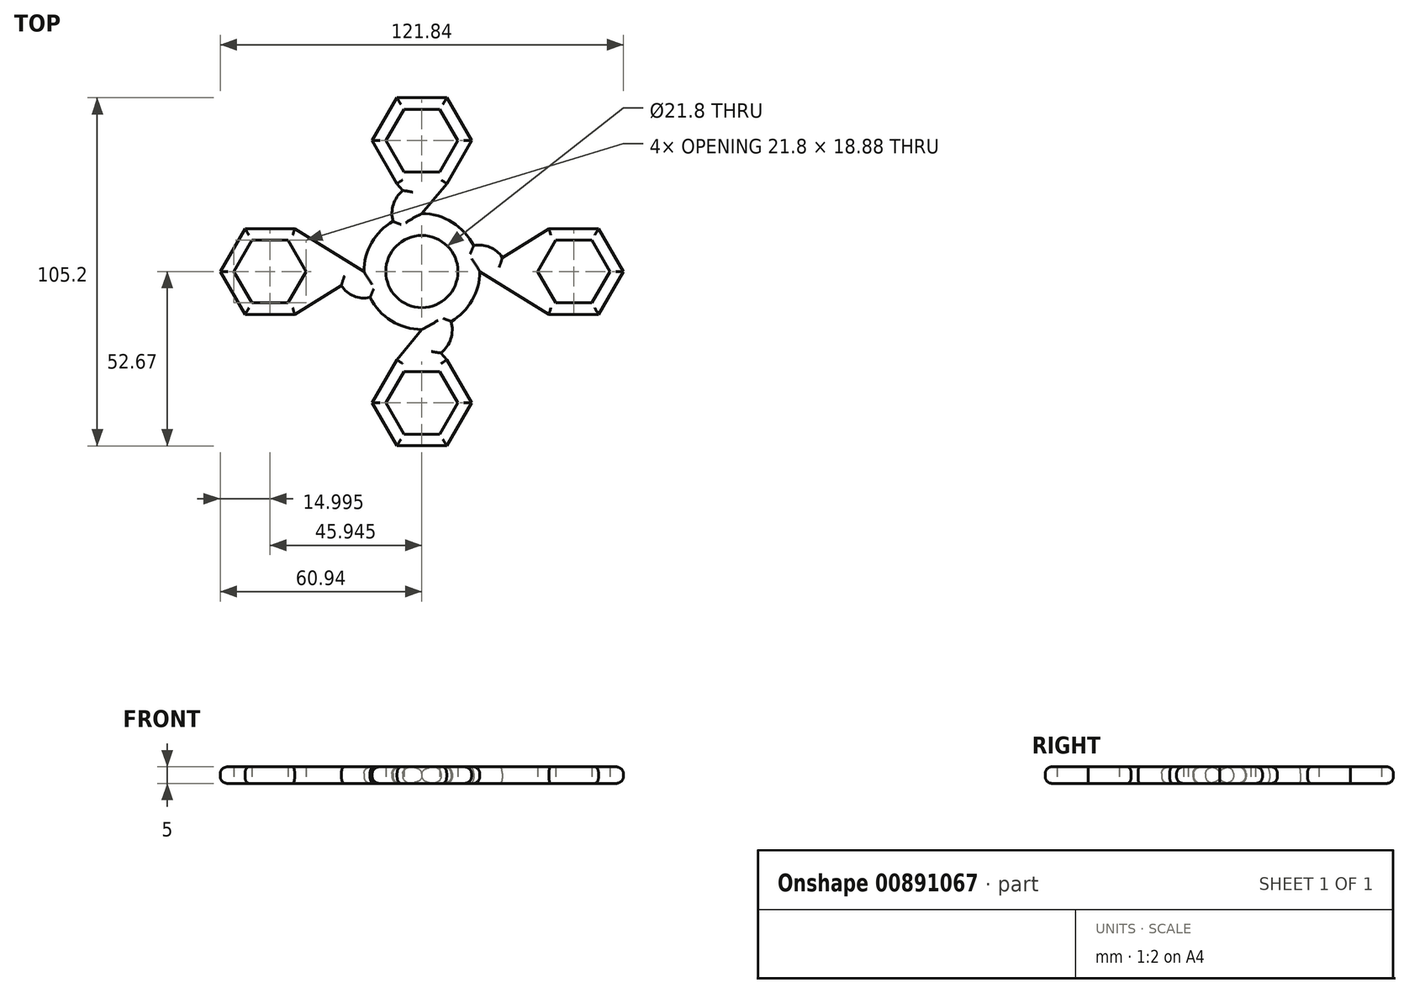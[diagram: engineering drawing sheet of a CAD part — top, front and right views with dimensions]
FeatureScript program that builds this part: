
annotation { "Feature Type Name" : "Feature", "Feature Type Description" : "" }
export const myFeature = defineFeature(function(context is Context, id is Id, definition is map)
    precondition{}
    {
        {
            var Q0;
            Q0=qCreatedBy(makeId("Top.planeOp"),FACE);
            var sketch = newSketch(context, id + "F0", { "sketchPlane" : qUnion([Q0])});
            skCircle(sketch, "E0", {"center": v(0, 0) * mm, "radius": 10.9 * mm});
            skCircle(sketch, "E1.cCircle", {"center": v(45.9, 0) * mm, "radius": 9.44 * mm, "construction": true});
            skLineSegment(sketch, "E1.0", {"start": v(40.45, 9.44) * mm, "end": v(51.35, 9.44) * mm});
            skLineSegment(sketch, "E1.1", {"start": v(51.35, 9.44) * mm, "end": v(56.8, 0) * mm});
            skLineSegment(sketch, "E1.2", {"start": v(56.8, 0) * mm, "end": v(51.35, -9.44) * mm});
            skLineSegment(sketch, "E1.3", {"start": v(51.35, -9.44) * mm, "end": v(40.45, -9.44) * mm});
            skLineSegment(sketch, "E1.4", {"start": v(40.45, -9.44) * mm, "end": v(35, 0) * mm});
            skLineSegment(sketch, "E1.5", {"start": v(35, 0) * mm, "end": v(40.45, 9.44) * mm});
            skPoint(sketch, "E1.0.midPoint", {"position": v(45.9, 9.44) * mm});
            skLineSegment(sketch, "E2", {"start": v(0, 0) * mm, "end": v(35, 0) * mm});
            skLineSegment(sketch, "E3", {"start": v(0, 0) * mm, "end": v(-35, 0) * mm});
            skCircle(sketch, "E4.cCircle", {"center": v(-45.94, 0) * mm, "radius": 9.44 * mm, "construction": true});
            skLineSegment(sketch, "E4.0", {"start": v(-51.4, 9.44) * mm, "end": v(-40.5, 9.44) * mm});
            skLineSegment(sketch, "E4.1", {"start": v(-40.5, 9.44) * mm, "end": v(-35.04, 0) * mm});
            skLineSegment(sketch, "E4.2", {"start": v(-35.04, 0) * mm, "end": v(-40.5, -9.44) * mm});
            skLineSegment(sketch, "E4.3", {"start": v(-40.5, -9.44) * mm, "end": v(-51.4, -9.44) * mm});
            skLineSegment(sketch, "E4.4", {"start": v(-51.4, -9.44) * mm, "end": v(-56.84, 0) * mm});
            skLineSegment(sketch, "E4.5", {"start": v(-56.84, 0) * mm, "end": v(-51.4, 9.44) * mm});
            skPoint(sketch, "E4.0.midPoint", {"position": v(-45.94, 9.44) * mm});
            skLineSegment(sketch, "E5", {"start": v(0, 0) * mm, "end": v(0, 30) * mm});
            skLineSegment(sketch, "E6", {"start": v(0, 30) * mm, "end": v(0, -30) * mm});
            skCircle(sketch, "E7.cCircle", {"center": v(0, -39.68) * mm, "radius": 9.44 * mm, "construction": true});
            skLineSegment(sketch, "E7.0", {"start": v(-5.45, -30.24) * mm, "end": v(5.45, -30.24) * mm});
            skLineSegment(sketch, "E7.1", {"start": v(5.45, -30.24) * mm, "end": v(10.9, -39.68) * mm});
            skLineSegment(sketch, "E7.2", {"start": v(10.9, -39.68) * mm, "end": v(5.45, -49.12) * mm});
            skLineSegment(sketch, "E7.3", {"start": v(5.45, -49.12) * mm, "end": v(-5.45, -49.12) * mm});
            skLineSegment(sketch, "E7.4", {"start": v(-5.45, -49.12) * mm, "end": v(-10.9, -39.68) * mm});
            skLineSegment(sketch, "E7.5", {"start": v(-10.9, -39.68) * mm, "end": v(-5.45, -30.24) * mm});
            skPoint(sketch, "E7.0.midPoint", {"position": v(0, -30.24) * mm});
            skCircle(sketch, "E8.cCircle", {"center": v(0, 39.54) * mm, "radius": 9.44 * mm, "construction": true});
            skLineSegment(sketch, "E8.0", {"start": v(-5.45, 48.98) * mm, "end": v(5.45, 48.98) * mm});
            skLineSegment(sketch, "E8.1", {"start": v(5.45, 48.98) * mm, "end": v(10.9, 39.54) * mm});
            skLineSegment(sketch, "E8.2", {"start": v(10.9, 39.54) * mm, "end": v(5.45, 30.1) * mm});
            skLineSegment(sketch, "E8.3", {"start": v(5.45, 30.1) * mm, "end": v(-5.45, 30.1) * mm});
            skLineSegment(sketch, "E8.4", {"start": v(-5.45, 30.1) * mm, "end": v(-10.9, 39.54) * mm});
            skLineSegment(sketch, "E8.5", {"start": v(-10.9, 39.54) * mm, "end": v(-5.45, 48.98) * mm});
            skPoint(sketch, "E8.0.midPoint", {"position": v(0, 48.98) * mm});
            skCircle(sketch, "E9", {"center": v(0, 0) * mm, "radius": 17.5 * mm});
            skCircle(sketch, "E10.cCircle", {"center": v(-45.94, 0) * mm, "radius": 13 * mm, "construction": true});
            skLineSegment(sketch, "E10.0", {"start": v(-53.44, 13) * mm, "end": v(-38.44, 13) * mm});
            skLineSegment(sketch, "E10.1", {"start": v(-38.44, 13) * mm, "end": v(-30.94, 0) * mm});
            skLineSegment(sketch, "E10.2", {"start": v(-30.94, 0) * mm, "end": v(-38.44, -13) * mm});
            skLineSegment(sketch, "E10.3", {"start": v(-38.44, -13) * mm, "end": v(-53.44, -13) * mm});
            skLineSegment(sketch, "E10.4", {"start": v(-53.44, -13) * mm, "end": v(-60.94, 0) * mm});
            skLineSegment(sketch, "E10.5", {"start": v(-60.94, 0) * mm, "end": v(-53.44, 13) * mm});
            skPoint(sketch, "E10.0.midPoint", {"position": v(-45.94, 13) * mm});
            skCircle(sketch, "E11.cCircle", {"center": v(0, 39.54) * mm, "radius": 13 * mm, "construction": true});
            skLineSegment(sketch, "E11.0", {"start": v(-7.5, 52.53) * mm, "end": v(7.5, 52.53) * mm});
            skLineSegment(sketch, "E11.1", {"start": v(7.5, 52.53) * mm, "end": v(15, 39.54) * mm});
            skLineSegment(sketch, "E11.2", {"start": v(15, 39.54) * mm, "end": v(7.5, 26.55) * mm});
            skLineSegment(sketch, "E11.3", {"start": v(7.5, 26.55) * mm, "end": v(-7.5, 26.55) * mm});
            skLineSegment(sketch, "E11.4", {"start": v(-7.5, 26.55) * mm, "end": v(-15, 39.54) * mm});
            skLineSegment(sketch, "E11.5", {"start": v(-15, 39.54) * mm, "end": v(-7.5, 52.53) * mm});
            skPoint(sketch, "E11.0.midPoint", {"position": v(0, 52.53) * mm});
            skCircle(sketch, "E12.cCircle", {"center": v(45.9, 0) * mm, "radius": 13 * mm, "construction": true});
            skLineSegment(sketch, "E12.0", {"start": v(38.4, 13) * mm, "end": v(53.4, 13) * mm});
            skLineSegment(sketch, "E12.1", {"start": v(53.4, 13) * mm, "end": v(60.9, 0) * mm});
            skLineSegment(sketch, "E12.2", {"start": v(60.9, 0) * mm, "end": v(53.4, -13) * mm});
            skLineSegment(sketch, "E12.3", {"start": v(53.4, -13) * mm, "end": v(38.4, -13) * mm});
            skLineSegment(sketch, "E12.4", {"start": v(38.4, -13) * mm, "end": v(30.9, 0) * mm});
            skLineSegment(sketch, "E12.5", {"start": v(30.9, 0) * mm, "end": v(38.4, 13) * mm});
            skPoint(sketch, "E12.0.midPoint", {"position": v(45.9, 13) * mm});
            skCircle(sketch, "E13.cCircle", {"center": v(0, -39.68) * mm, "radius": 13 * mm, "construction": true});
            skLineSegment(sketch, "E13.0", {"start": v(-7.5, -26.69) * mm, "end": v(7.5, -26.69) * mm});
            skLineSegment(sketch, "E13.1", {"start": v(7.5, -26.69) * mm, "end": v(15, -39.68) * mm});
            skLineSegment(sketch, "E13.2", {"start": v(15, -39.68) * mm, "end": v(7.5, -52.67) * mm});
            skLineSegment(sketch, "E13.3", {"start": v(7.5, -52.67) * mm, "end": v(-7.5, -52.67) * mm});
            skLineSegment(sketch, "E13.4", {"start": v(-7.5, -52.67) * mm, "end": v(-15, -39.68) * mm});
            skLineSegment(sketch, "E13.5", {"start": v(-15, -39.68) * mm, "end": v(-7.5, -26.69) * mm});
            skPoint(sketch, "E13.0.midPoint", {"position": v(0, -26.69) * mm});
            skLineSegment(sketch, "E14", {"start": v(-7.5, 26.55) * mm, "end": v(0, 17.5) * mm});
            skLineSegment(sketch, "E15", {"start": v(0, 17.5) * mm, "end": v(7.5, 26.55) * mm});
            skLineSegment(sketch, "E16", {"start": v(-7.5, -26.69) * mm, "end": v(0, -17.5) * mm});
            skLineSegment(sketch, "E17", {"start": v(0, -17.5) * mm, "end": v(7.5, -26.69) * mm});
            skLineSegment(sketch, "E18", {"start": v(38.4, -13) * mm, "end": v(17.5, 0) * mm});
            skLineSegment(sketch, "E19", {"start": v(17.5, 0) * mm, "end": v(38.4, 13) * mm});
            skLineSegment(sketch, "E20", {"start": v(-17.5, 0) * mm, "end": v(-38.44, -13) * mm});
            skLineSegment(sketch, "E21", {"start": v(-17.5, 0) * mm, "end": v(-38.44, 13) * mm});
            skLineSegment(sketch, "E22", {"start": v(-17.5, 0) * mm, "end": v(-22.5, 0) * mm});
            skLineSegment(sketch, "E23", {"start": v(17.5, 0) * mm, "end": v(22.5, 0) * mm});
            skArc(sketch, "E24", {"start": v(0, -26.69) * mm, "mid": v(7.3, -23.08) * mm, "end": v(8.86, -15.09) * mm});
            skArc(sketch, "E25", {"start": v(0, -26.69) * mm, "mid": v(-7.3, -23.08) * mm, "end": v(-8.86, -15.09) * mm});
            skArc(sketch, "E26", {"start": v(0, 26.55) * mm, "mid": v(7.18, 23) * mm, "end": v(8.74, 15.16) * mm});
            skArc(sketch, "E27", {"start": v(0, 26.55) * mm, "mid": v(-7.18, 23) * mm, "end": v(-8.74, 15.16) * mm});
            skPoint(sketch, "E28", {"position": v(27.95, -6.5) * mm});
            skPoint(sketch, "E29", {"position": v(27.95, 6.5) * mm});
            skLineSegment(sketch, "E30", {"start": v(17.5, 0) * mm, "end": v(25.5, 0) * mm});
            skLineSegment(sketch, "E31", {"start": v(-17.5, 0) * mm, "end": v(-25.5, 0) * mm});
            skArc(sketch, "E32", {"start": v(25.5, 0) * mm, "mid": v(22.47, -6.27) * mm, "end": v(15.67, -7.79) * mm});
            skArc(sketch, "E33", {"start": v(25.5, 0) * mm, "mid": v(22.47, 6.27) * mm, "end": v(15.67, 7.79) * mm});
            skArc(sketch, "E34", {"start": v(-25.5, 0) * mm, "mid": v(-22.47, -6.27) * mm, "end": v(-15.67, -7.79) * mm});
            skArc(sketch, "E35", {"start": v(-25.5, 0) * mm, "mid": v(-22.47, 6.27) * mm, "end": v(-15.67, 7.79) * mm});
            skSolve(sketch);
        }
        {
            var Q0;
            Q0=makeQuery(id+"F0.imprint","IMPRINT",FACE,{"disambiguationData":[TD([[makeQuery(id+"F0.imprint","IMPRINT",EDGE,{"derivedFrom":sQuery(id+"F0.wireOp",EDGE,"E4.0")}),1.0]])]});
            var Q1;
            {var subQ4=sQuery(id+"F0.wireOp",EDGE,"E0");var subQ6=sQuery(id+"F0.wireOp",EDGE,"E5");var subQ7=makeQuery(id+"F0.imprint","INTERSECT",VERTEX,{"derivedFrom":[subQ4,subQ6]});Q1=makeQuery(id+"F0.imprint","IMPRINT",FACE,{"disambiguationData":[TD([[makeQuery(id+"F0.imprint","IMPRINT",EDGE,{"disambiguationData":[TD([[subQ7,1.0]])],"derivedFrom":subQ4}),-1.0]])]});}
            var Q2;
            {var subQ3=sQuery(id+"F0.wireOp",EDGE,"E0");var subQ6=sQuery(id+"F0.wireOp",EDGE,"E2");var subQ8=makeQuery(id+"F0.imprint","INTERSECT",VERTEX,{"derivedFrom":[subQ3,subQ6]});Q2=makeQuery(id+"F0.imprint","IMPRINT",FACE,{"disambiguationData":[TD([[makeQuery(id+"F0.imprint","IMPRINT",EDGE,{"disambiguationData":[TD([[subQ8,1.0]])],"derivedFrom":subQ3}),-1.0]])]});}
            var Q3;
            {var subQ1=sQuery(id+"F0.wireOp",EDGE,"E5");var subQ4=sQuery(id+"F0.wireOp",EDGE,"E0");var subQ5=makeQuery(id+"F0.imprint","INTERSECT",VERTEX,{"derivedFrom":[subQ4,subQ1]});Q3=makeQuery(id+"F0.imprint","IMPRINT",FACE,{"disambiguationData":[TD([[makeQuery(id+"F0.imprint","IMPRINT",EDGE,{"disambiguationData":[TD([[subQ5,-1.0]])],"derivedFrom":subQ4}),-1.0]])]});}
            var Q4;
            Q4=makeQuery(id+"F0.imprint","IMPRINT",FACE,{"disambiguationData":[TD([[makeQuery(id+"F0.imprint","IMPRINT",EDGE,{"derivedFrom":sQuery(id+"F0.wireOp",EDGE,"E8.0")}),1.0]])]});
            var Q5;
            Q5=makeQuery(id+"F0.imprint","IMPRINT",FACE,{"disambiguationData":[TD([[makeQuery(id+"F0.imprint","IMPRINT",EDGE,{"derivedFrom":sQuery(id+"F0.wireOp",EDGE,"E1.0")}),1.0]])]});
            var Q6;
            Q6=makeQuery(id+"F0.imprint","IMPRINT",FACE,{"disambiguationData":[TD([[makeQuery(id+"F0.imprint","IMPRINT",EDGE,{"derivedFrom":sQuery(id+"F0.wireOp",EDGE,"E7.0")}),1.0]])]});
            var Q7;
            {var subQ0=sQuery(id+"F0.wireOp",EDGE,"E15");var subQ3=sQuery(id+"F0.wireOp",EDGE,"E26");var subQ6=makeQuery(id+"F0.imprint","INTERSECT",VERTEX,{"derivedFrom":[subQ0,subQ3]});Q7=qUnion([makeQuery(id+"F0.imprint","IMPRINT",FACE,{"disambiguationData":[TD([[makeQuery(id+"F0.imprint","IMPRINT",EDGE,{"disambiguationData":[TD([[subQ6,1.0]])],"derivedFrom":subQ0}),1.0]])]}),makeQuery(id+"F0.imprint","IMPRINT",FACE,{"disambiguationData":[TD([[makeQuery(id+"F0.imprint","IMPRINT",EDGE,{"disambiguationData":[TD([[subQ6,-1.0]])],"derivedFrom":subQ0}),1.0]])]})]);}
            var Q8;
            {var subQ0=sQuery(id+"F0.wireOp",EDGE,"E27");var subQ4=sQuery(id+"F0.wireOp",EDGE,"E14");var subQ6=makeQuery(id+"F0.imprint","INTERSECT",VERTEX,{"derivedFrom":[subQ4,subQ0]});Q8=qUnion([makeQuery(id+"F0.imprint","IMPRINT",FACE,{"disambiguationData":[TD([[makeQuery(id+"F0.imprint","IMPRINT",EDGE,{"disambiguationData":[TD([[subQ6,-1.0]])],"derivedFrom":subQ4}),1.0]])]}),makeQuery(id+"F0.imprint","IMPRINT",FACE,{"disambiguationData":[TD([[makeQuery(id+"F0.imprint","IMPRINT",EDGE,{"disambiguationData":[TD([[subQ6,1.0]])],"derivedFrom":subQ4}),1.0]])]})]);}
            var Q9;
            {var subQ0=sQuery(id+"F0.wireOp",EDGE,"E17");var subQ3=sQuery(id+"F0.wireOp",EDGE,"E24");var subQ6=makeQuery(id+"F0.imprint","INTERSECT",VERTEX,{"derivedFrom":[subQ0,subQ3]});Q9=qUnion([makeQuery(id+"F0.imprint","IMPRINT",FACE,{"disambiguationData":[TD([[makeQuery(id+"F0.imprint","IMPRINT",EDGE,{"disambiguationData":[TD([[subQ6,1.0]])],"derivedFrom":subQ0}),-1.0]])]}),makeQuery(id+"F0.imprint","IMPRINT",FACE,{"disambiguationData":[TD([[makeQuery(id+"F0.imprint","IMPRINT",EDGE,{"disambiguationData":[TD([[subQ6,-1.0]])],"derivedFrom":subQ0}),-1.0]])]})]);}
            var Q10;
            {var subQ0=sQuery(id+"F0.wireOp",EDGE,"E16");var subQ3=sQuery(id+"F0.wireOp",EDGE,"E25");var subQ6=makeQuery(id+"F0.imprint","INTERSECT",VERTEX,{"derivedFrom":[subQ0,subQ3]});Q10=qUnion([makeQuery(id+"F0.imprint","IMPRINT",FACE,{"disambiguationData":[TD([[makeQuery(id+"F0.imprint","IMPRINT",EDGE,{"disambiguationData":[TD([[subQ6,1.0]])],"derivedFrom":subQ0}),-1.0]])]}),makeQuery(id+"F0.imprint","IMPRINT",FACE,{"disambiguationData":[TD([[makeQuery(id+"F0.imprint","IMPRINT",EDGE,{"disambiguationData":[TD([[subQ6,-1.0]])],"derivedFrom":subQ0}),-1.0]])]})]);}
            var Q11;
            {var subQ3=sQuery(id+"F0.wireOp",EDGE,"E10.2");Q11=makeQuery(id+"F0.imprint","IMPRINT",FACE,{"disambiguationData":[TD([[makeQuery(id+"F0.imprint","IMPRINT",EDGE,{"derivedFrom":subQ3}),1.0]])]});}
            var Q12;
            {var subQ3=sQuery(id+"F0.wireOp",EDGE,"E10.1");Q12=makeQuery(id+"F0.imprint","IMPRINT",FACE,{"disambiguationData":[TD([[makeQuery(id+"F0.imprint","IMPRINT",EDGE,{"derivedFrom":subQ3}),1.0]])]});}
            var Q13;
            {var subQ3=sQuery(id+"F0.wireOp",EDGE,"E12.4");Q13=makeQuery(id+"F0.imprint","IMPRINT",FACE,{"disambiguationData":[TD([[makeQuery(id+"F0.imprint","IMPRINT",EDGE,{"derivedFrom":subQ3}),1.0]])]});}
            var Q14;
            {var subQ3=sQuery(id+"F0.wireOp",EDGE,"E12.5");Q14=makeQuery(id+"F0.imprint","IMPRINT",FACE,{"disambiguationData":[TD([[makeQuery(id+"F0.imprint","IMPRINT",EDGE,{"derivedFrom":subQ3}),1.0]])]});}
            var Q15;
            {var subQ1=sQuery(id+"F0.wireOp",EDGE,"E9");var subQ3=sQuery(id+"F0.wireOp",EDGE,"Ubq4kfX4-oC6w-lFNq-I3q3-88G8mSC7eADd");var subQ4=makeQuery(id+"F0.imprint","INTERSECT",VERTEX,{"derivedFrom":[subQ1,subQ3]});Q15=makeQuery(id+"F0.imprint","IMPRINT",FACE,{"disambiguationData":[TD([[makeQuery(id+"F0.imprint","IMPRINT",EDGE,{"disambiguationData":[TD([[subQ4,1.0]])],"derivedFrom":subQ3}),1.0]])]});}
            var Q16;
            {var subQ0=sQuery(id+"F0.wireOp",EDGE,"E22");Q16=makeQuery(id+"F0.imprint","IMPRINT",FACE,{"disambiguationData":[TD([[makeQuery(id+"F0.imprint","IMPRINT",EDGE,{"derivedFrom":subQ0}),1.0]])]});}
            var Q17;
            {var subQ1=sQuery(id+"F0.wireOp",EDGE,"E9");var subQ3=sQuery(id+"F0.wireOp",EDGE,"DwJBgmho-QLLy-2BSY-i2pv-QXPFVA0WSpVR");var subQ4=makeQuery(id+"F0.imprint","INTERSECT",VERTEX,{"derivedFrom":[subQ1,subQ3]});Q17=makeQuery(id+"F0.imprint","IMPRINT",FACE,{"disambiguationData":[TD([[makeQuery(id+"F0.imprint","IMPRINT",EDGE,{"disambiguationData":[TD([[subQ4,1.0]])],"derivedFrom":subQ3}),-1.0]])]});}
            var Q18;
            {var subQ0=sQuery(id+"F0.wireOp",EDGE,"E22");Q18=makeQuery(id+"F0.imprint","IMPRINT",FACE,{"disambiguationData":[TD([[makeQuery(id+"F0.imprint","IMPRINT",EDGE,{"derivedFrom":subQ0}),-1.0]])]});}
            var Q19;
            {var subQ1=sQuery(id+"F0.wireOp",EDGE,"E9");var subQ3=sQuery(id+"F0.wireOp",EDGE,"ud0qLV0T-u8xm-Fev3-eQ3F-uhF6uLOVjt4z");var subQ4=makeQuery(id+"F0.imprint","INTERSECT",VERTEX,{"derivedFrom":[subQ1,subQ3]});Q19=makeQuery(id+"F0.imprint","IMPRINT",FACE,{"disambiguationData":[TD([[makeQuery(id+"F0.imprint","IMPRINT",EDGE,{"disambiguationData":[TD([[subQ4,1.0]])],"derivedFrom":subQ3}),1.0]])]});}
            var Q20;
            {var subQ0=sQuery(id+"F0.wireOp",EDGE,"E23");Q20=makeQuery(id+"F0.imprint","IMPRINT",FACE,{"disambiguationData":[TD([[makeQuery(id+"F0.imprint","IMPRINT",EDGE,{"derivedFrom":subQ0}),1.0]])]});}
            var Q21;
            {var subQ0=sQuery(id+"F0.wireOp",EDGE,"E23");Q21=makeQuery(id+"F0.imprint","IMPRINT",FACE,{"disambiguationData":[TD([[makeQuery(id+"F0.imprint","IMPRINT",EDGE,{"derivedFrom":subQ0}),-1.0]])]});}
            var Q22;
            {var subQ1=sQuery(id+"F0.wireOp",EDGE,"E9");var subQ3=sQuery(id+"F0.wireOp",EDGE,"Qvp8duAn-RZq8-JCAh-Xm4F-s16nUtTtBb3N");var subQ4=makeQuery(id+"F0.imprint","INTERSECT",VERTEX,{"derivedFrom":[subQ1,subQ3]});Q22=makeQuery(id+"F0.imprint","IMPRINT",FACE,{"disambiguationData":[TD([[makeQuery(id+"F0.imprint","IMPRINT",EDGE,{"disambiguationData":[TD([[subQ4,1.0]])],"derivedFrom":subQ3}),-1.0]])]});}
            var Q23;
            {var subQ1=sQuery(id+"F0.wireOp",EDGE,"E9");var subQ3=sQuery(id+"F0.wireOp",EDGE,"c0TzAWUU-cxwK-REM3-tjBK-XptVohU1FABc");var subQ4=makeQuery(id+"F0.imprint","INTERSECT",VERTEX,{"derivedFrom":[subQ1,subQ3]});Q23=makeQuery(id+"F0.imprint","IMPRINT",FACE,{"disambiguationData":[TD([[makeQuery(id+"F0.imprint","IMPRINT",EDGE,{"disambiguationData":[TD([[subQ4,1.0]])],"derivedFrom":subQ3}),-1.0]])]});}
            var Q24;
            {var subQ1=sQuery(id+"F0.wireOp",EDGE,"E9");var subQ3=sQuery(id+"F0.wireOp",EDGE,"k8nK72Cl-iwD2-dbTf-OI5i-pcYR12xtiAX6");var subQ4=makeQuery(id+"F0.imprint","INTERSECT",VERTEX,{"derivedFrom":[subQ1,subQ3]});Q24=makeQuery(id+"F0.imprint","IMPRINT",FACE,{"disambiguationData":[TD([[makeQuery(id+"F0.imprint","IMPRINT",EDGE,{"disambiguationData":[TD([[subQ4,1.0]])],"derivedFrom":subQ3}),1.0]])]});}
            var Q25;
            {var subQ0=sQuery(id+"F0.wireOp",EDGE,"E27");var subQ3=sQuery(id+"F0.wireOp",EDGE,"E14");var subQ5=makeQuery(id+"F0.imprint","INTERSECT",VERTEX,{"derivedFrom":[subQ3,subQ0]});Q25=makeQuery(id+"F0.imprint","IMPRINT",FACE,{"disambiguationData":[TD([[makeQuery(id+"F0.imprint","IMPRINT",EDGE,{"disambiguationData":[TD([[subQ5,-1.0]])],"derivedFrom":subQ3}),1.0]])]});}
            var Q26;
            {var subQ0=sQuery(id+"F0.wireOp",EDGE,"E26");var subQ3=sQuery(id+"F0.wireOp",EDGE,"E15");var subQ5=makeQuery(id+"F0.imprint","INTERSECT",VERTEX,{"derivedFrom":[subQ3,subQ0]});Q26=makeQuery(id+"F0.imprint","IMPRINT",FACE,{"disambiguationData":[TD([[makeQuery(id+"F0.imprint","IMPRINT",EDGE,{"disambiguationData":[TD([[subQ5,1.0]])],"derivedFrom":subQ3}),1.0]])]});}
            var Q27;
            {var subQ0=sQuery(id+"F0.wireOp",EDGE,"E16");var subQ3=sQuery(id+"F0.wireOp",EDGE,"E25");var subQ5=makeQuery(id+"F0.imprint","INTERSECT",VERTEX,{"derivedFrom":[subQ0,subQ3]});Q27=makeQuery(id+"F0.imprint","IMPRINT",FACE,{"disambiguationData":[TD([[makeQuery(id+"F0.imprint","IMPRINT",EDGE,{"disambiguationData":[TD([[subQ5,-1.0]])],"derivedFrom":subQ3}),-1.0]])]});}
            var Q28;
            {var subQ1=sQuery(id+"F0.wireOp",EDGE,"E9");var subQ3=sQuery(id+"F0.wireOp",EDGE,"E24");var subQ4=makeQuery(id+"F0.imprint","INTERSECT",VERTEX,{"derivedFrom":[subQ1,subQ3]});Q28=makeQuery(id+"F0.imprint","IMPRINT",FACE,{"disambiguationData":[TD([[makeQuery(id+"F0.imprint","IMPRINT",EDGE,{"disambiguationData":[TD([[subQ4,1.0]])],"derivedFrom":subQ3}),1.0]])]});}
            var Q29;
            {var subQ1=sQuery(id+"F0.wireOp",EDGE,"E9");var subQ3=sQuery(id+"F0.wireOp",EDGE,"E32");var subQ4=makeQuery(id+"F0.imprint","INTERSECT",VERTEX,{"derivedFrom":[subQ1,subQ3]});Q29=makeQuery(id+"F0.imprint","IMPRINT",FACE,{"disambiguationData":[TD([[makeQuery(id+"F0.imprint","IMPRINT",EDGE,{"disambiguationData":[TD([[subQ4,1.0]])],"derivedFrom":subQ3}),-1.0]])]});}
            var Q30;
            {var subQ0=sQuery(id+"F0.wireOp",EDGE,"E19");var subQ3=sQuery(id+"F0.wireOp",EDGE,"E33");var subQ5=makeQuery(id+"F0.imprint","INTERSECT",VERTEX,{"derivedFrom":[subQ0,subQ3]});Q30=makeQuery(id+"F0.imprint","IMPRINT",FACE,{"disambiguationData":[TD([[makeQuery(id+"F0.imprint","IMPRINT",EDGE,{"disambiguationData":[TD([[subQ5,-1.0]])],"derivedFrom":subQ3}),1.0]])]});}
            var Q31;
            {var subQ1=sQuery(id+"F0.wireOp",EDGE,"E2");var subQ3=makeQuery(id+"F0.imprint","IMPRINT",VERTEX,{"derivedFrom":subQ1});Q31=makeQuery(id+"F0.imprint","IMPRINT",FACE,{"disambiguationData":[TD([[makeQuery(id+"F0.imprint","IMPRINT",EDGE,{"disambiguationData":[TD([[subQ3,-1.0]])],"derivedFrom":subQ1}),1.0]])]});}
            var Q32;
            {var subQ1=sQuery(id+"F0.wireOp",EDGE,"E2");var subQ3=makeQuery(id+"F0.imprint","IMPRINT",VERTEX,{"derivedFrom":subQ1});Q32=makeQuery(id+"F0.imprint","IMPRINT",FACE,{"disambiguationData":[TD([[makeQuery(id+"F0.imprint","IMPRINT",EDGE,{"disambiguationData":[TD([[subQ3,-1.0]])],"derivedFrom":subQ1}),-1.0]])]});}
            var Q33;
            {var subQ0=sQuery(id+"F0.wireOp",EDGE,"E34");var subQ3=sQuery(id+"F0.wireOp",EDGE,"E20");var subQ5=makeQuery(id+"F0.imprint","INTERSECT",VERTEX,{"derivedFrom":[subQ3,subQ0]});Q33=makeQuery(id+"F0.imprint","IMPRINT",FACE,{"disambiguationData":[TD([[makeQuery(id+"F0.imprint","IMPRINT",EDGE,{"disambiguationData":[TD([[subQ5,-1.0]])],"derivedFrom":subQ0}),1.0]])]});}
            var Q34;
            {var subQ2=sQuery(id+"F0.wireOp",EDGE,"E3");var subQ6=sQuery(id+"F0.wireOp",EDGE,"E0");var subQ8=makeQuery(id+"F0.imprint","INTERSECT",VERTEX,{"derivedFrom":[subQ6,subQ2]});Q34=makeQuery(id+"F0.imprint","IMPRINT",FACE,{"disambiguationData":[TD([[makeQuery(id+"F0.imprint","IMPRINT",EDGE,{"disambiguationData":[TD([[subQ8,-1.0]])],"derivedFrom":subQ6}),-1.0]])]});}
            var Q35;
            {var subQ0=sQuery(id+"F0.wireOp",EDGE,"E3");var subQ1=makeQuery(id+"F0.imprint","IMPRINT",VERTEX,{"derivedFrom":subQ0});Q35=makeQuery(id+"F0.imprint","IMPRINT",FACE,{"disambiguationData":[TD([[makeQuery(id+"F0.imprint","IMPRINT",EDGE,{"disambiguationData":[TD([[subQ1,-1.0]])],"derivedFrom":subQ0}),1.0]])]});}
            var Q36;
            {var subQ0=sQuery(id+"F0.wireOp",EDGE,"E3");var subQ1=makeQuery(id+"F0.imprint","IMPRINT",VERTEX,{"derivedFrom":subQ0});Q36=makeQuery(id+"F0.imprint","IMPRINT",FACE,{"disambiguationData":[TD([[makeQuery(id+"F0.imprint","IMPRINT",EDGE,{"disambiguationData":[TD([[subQ1,-1.0]])],"derivedFrom":subQ0}),-1.0]])]});}
            var Q37;
            {var subQ0=sQuery(id+"F0.wireOp",EDGE,"E35");var subQ3=sQuery(id+"F0.wireOp",EDGE,"E21");var subQ5=makeQuery(id+"F0.imprint","INTERSECT",VERTEX,{"derivedFrom":[subQ3,subQ0]});Q37=makeQuery(id+"F0.imprint","IMPRINT",FACE,{"disambiguationData":[TD([[makeQuery(id+"F0.imprint","IMPRINT",EDGE,{"disambiguationData":[TD([[subQ5,-1.0]])],"derivedFrom":subQ0}),-1.0]])]});}
            var Q38;
            {var subQ0=sQuery(id+"F0.wireOp",EDGE,"E14");var subQ3=sQuery(id+"F0.wireOp",EDGE,"E27");var subQ5=makeQuery(id+"F0.imprint","INTERSECT",VERTEX,{"derivedFrom":[subQ0,subQ3]});Q38=makeQuery(id+"F0.imprint","IMPRINT",FACE,{"disambiguationData":[TD([[makeQuery(id+"F0.imprint","IMPRINT",EDGE,{"disambiguationData":[TD([[subQ5,-1.0]])],"derivedFrom":subQ3}),1.0]])]});}
            var Q39;
            {var subQ1=sQuery(id+"F0.wireOp",EDGE,"E9");var subQ3=sQuery(id+"F0.wireOp",EDGE,"E26");var subQ4=makeQuery(id+"F0.imprint","INTERSECT",VERTEX,{"derivedFrom":[subQ1,subQ3]});Q39=makeQuery(id+"F0.imprint","IMPRINT",FACE,{"disambiguationData":[TD([[makeQuery(id+"F0.imprint","IMPRINT",EDGE,{"disambiguationData":[TD([[subQ4,1.0]])],"derivedFrom":subQ3}),-1.0]])]});}
            extrude(context, id + "F1", {"entities" : qUnion([Q0, Q1, Q2, Q3, Q4, Q5, Q6, Q7, Q8, Q9, Q10, Q11, Q12, Q13, Q14, Q15, Q16, Q17, Q18, Q19, Q20, Q21, Q22, Q23, Q24, Q25, Q26, Q27, Q28, Q29, Q30, Q31, Q32, Q33, Q34, Q35, Q36, Q37, Q38, Q39]), "depth" : 5 * mm, "offsetDistance" : 25 * mm});
        }
        {
            var Q0;
            Q0=makeQuery(id+"F1.opExtrude","CAP_EDGE",EDGE,{"disambiguationData":[OSD([sQuery(id+"F0.wireOp",EDGE,"E25")])],"isStart":false});
            var Q1;
            Q1=makeQuery(id+"F1.opExtrude","CAP_EDGE",EDGE,{"disambiguationData":[OSD([sQuery(id+"F0.wireOp",EDGE,"E16")])],"isStart":false});
            var Q2;
            Q2=makeQuery(id+"F1.opExtrude","CAP_EDGE",EDGE,{"disambiguationData":[OSD([sQuery(id+"F0.wireOp",EDGE,"E13.5")])],"isStart":false});
            var Q3;
            Q3=makeQuery(id+"F1.opExtrude","CAP_EDGE",EDGE,{"disambiguationData":[OSD([sQuery(id+"F0.wireOp",EDGE,"E13.4")])],"isStart":false});
            var Q4;
            Q4=makeQuery(id+"F1.opExtrude","CAP_EDGE",EDGE,{"disambiguationData":[OSD([sQuery(id+"F0.wireOp",EDGE,"E13.3")])],"isStart":false});
            var Q5;
            Q5=makeQuery(id+"F1.opExtrude","CAP_EDGE",EDGE,{"disambiguationData":[OSD([sQuery(id+"F0.wireOp",EDGE,"E13.2")])],"isStart":false});
            var Q6;
            Q6=makeQuery(id+"F1.opExtrude","CAP_EDGE",EDGE,{"disambiguationData":[OSD([sQuery(id+"F0.wireOp",EDGE,"E13.1")])],"isStart":false});
            var Q7;
            Q7=makeQuery(id+"F1.opExtrude","CAP_EDGE",EDGE,{"disambiguationData":[OSD([sQuery(id+"F0.wireOp",EDGE,"E17")])],"isStart":false});
            var Q8;
            Q8=makeQuery(id+"F1.opExtrude","CAP_EDGE",EDGE,{"disambiguationData":[OSD([sQuery(id+"F0.wireOp",EDGE,"E24")])],"isStart":false});
            fillet(context, id + "F2", {"entities" : qUnion([Q0, Q1, Q2, Q3, Q4, Q5, Q6, Q7, Q8]), "radius" : 2 * mm, "tangentPropagation" : true, "allowEdgeOverflow" : false});
        }
        {
            var Q0;
            Q0=makeQuery(id+"F1.opExtrude","CAP_EDGE",EDGE,{"disambiguationData":[OSD([sQuery(id+"F0.wireOp",EDGE,"E13.5")])],"isStart":true});
            var Q1;
            Q1=makeQuery(id+"F1.opExtrude","CAP_EDGE",EDGE,{"disambiguationData":[OSD([sQuery(id+"F0.wireOp",EDGE,"E16")])],"isStart":true});
            var Q2;
            Q2=makeQuery(id+"F1.opExtrude","CAP_EDGE",EDGE,{"disambiguationData":[OSD([sQuery(id+"F0.wireOp",EDGE,"E25")])],"isStart":true});
            var Q3;
            Q3=makeQuery(id+"F1.opExtrude","CAP_EDGE",EDGE,{"disambiguationData":[OSD([sQuery(id+"F0.wireOp",EDGE,"E24")])],"isStart":true});
            var Q4;
            Q4=makeQuery(id+"F1.opExtrude","CAP_EDGE",EDGE,{"disambiguationData":[OSD([sQuery(id+"F0.wireOp",EDGE,"E17")])],"isStart":true});
            var Q5;
            Q5=makeQuery(id+"F1.opExtrude","CAP_EDGE",EDGE,{"disambiguationData":[OSD([sQuery(id+"F0.wireOp",EDGE,"E13.1")])],"isStart":true});
            var Q6;
            Q6=makeQuery(id+"F1.opExtrude","CAP_EDGE",EDGE,{"disambiguationData":[OSD([sQuery(id+"F0.wireOp",EDGE,"E13.2")])],"isStart":true});
            var Q7;
            Q7=makeQuery(id+"F1.opExtrude","CAP_EDGE",EDGE,{"disambiguationData":[OSD([sQuery(id+"F0.wireOp",EDGE,"E13.3")])],"isStart":true});
            var Q8;
            Q8=makeQuery(id+"F1.opExtrude","CAP_EDGE",EDGE,{"disambiguationData":[OSD([sQuery(id+"F0.wireOp",EDGE,"E13.4")])],"isStart":true});
            fillet(context, id + "F3", {"entities" : qUnion([Q0, Q1, Q2, Q3, Q4, Q5, Q6, Q7, Q8]), "radius" : 2 * mm, "tangentPropagation" : true, "allowEdgeOverflow" : false});
        }
        {
            var Q0;
            {var subQ0=sQuery(id+"F0.wireOp",EDGE,"E9");Q0=makeQuery(id+"F1.opExtrude","CAP_EDGE",EDGE,{"disambiguationData":[OSD([subQ0]),TDD([makeQuery(id+"F0.imprint","IMPRINT",EDGE,{"disambiguationData":[TD([[makeQuery(id+"F0.imprint","INTERSECT",VERTEX,{"derivedFrom":[subQ0,sQuery(id+"F0.wireOp",EDGE,"E24")]}),-1.0]])],"derivedFrom":subQ0})])],"isStart":false});}
            var Q1;
            {var subQ0=sQuery(id+"F0.wireOp",EDGE,"E9");Q1=makeQuery(id+"F1.opExtrude","CAP_EDGE",EDGE,{"disambiguationData":[OSD([subQ0]),TDD([makeQuery(id+"F0.imprint","IMPRINT",EDGE,{"disambiguationData":[TD([[makeQuery(id+"F0.imprint","INTERSECT",VERTEX,{"derivedFrom":[subQ0,sQuery(id+"F0.wireOp",EDGE,"E24")]}),-1.0]])],"derivedFrom":subQ0})])],"isStart":true});}
            var Q2;
            Q2=makeQuery(id+"F1.opExtrude","CAP_EDGE",EDGE,{"disambiguationData":[OSD([sQuery(id+"F0.wireOp",EDGE,"E32")])],"isStart":false});
            var Q3;
            Q3=makeQuery(id+"F1.opExtrude","CAP_EDGE",EDGE,{"disambiguationData":[OSD([sQuery(id+"F0.wireOp",EDGE,"E32")])],"isStart":true});
            var Q4;
            Q4=makeQuery(id+"F1.opExtrude","CAP_EDGE",EDGE,{"disambiguationData":[OSD([sQuery(id+"F0.wireOp",EDGE,"E18")])],"isStart":false});
            var Q5;
            Q5=makeQuery(id+"F1.opExtrude","CAP_EDGE",EDGE,{"disambiguationData":[OSD([sQuery(id+"F0.wireOp",EDGE,"E18")])],"isStart":true});
            var Q6;
            Q6=makeQuery(id+"F1.opExtrude","CAP_EDGE",EDGE,{"disambiguationData":[OSD([sQuery(id+"F0.wireOp",EDGE,"E12.3")])],"isStart":true});
            var Q7;
            Q7=makeQuery(id+"F1.opExtrude","CAP_EDGE",EDGE,{"disambiguationData":[OSD([sQuery(id+"F0.wireOp",EDGE,"E12.3")])],"isStart":false});
            var Q8;
            Q8=makeQuery(id+"F1.opExtrude","CAP_EDGE",EDGE,{"disambiguationData":[OSD([sQuery(id+"F0.wireOp",EDGE,"E12.2")])],"isStart":true});
            var Q9;
            Q9=makeQuery(id+"F1.opExtrude","CAP_EDGE",EDGE,{"disambiguationData":[OSD([sQuery(id+"F0.wireOp",EDGE,"E12.2")])],"isStart":false});
            var Q10;
            Q10=makeQuery(id+"F1.opExtrude","CAP_EDGE",EDGE,{"disambiguationData":[OSD([sQuery(id+"F0.wireOp",EDGE,"E12.1")])],"isStart":false});
            var Q11;
            Q11=makeQuery(id+"F1.opExtrude","CAP_EDGE",EDGE,{"disambiguationData":[OSD([sQuery(id+"F0.wireOp",EDGE,"E12.1")])],"isStart":true});
            var Q12;
            Q12=makeQuery(id+"F1.opExtrude","CAP_EDGE",EDGE,{"disambiguationData":[OSD([sQuery(id+"F0.wireOp",EDGE,"E12.0")])],"isStart":true});
            var Q13;
            Q13=makeQuery(id+"F1.opExtrude","CAP_EDGE",EDGE,{"disambiguationData":[OSD([sQuery(id+"F0.wireOp",EDGE,"E12.0")])],"isStart":false});
            var Q14;
            Q14=makeQuery(id+"F1.opExtrude","CAP_EDGE",EDGE,{"disambiguationData":[OSD([sQuery(id+"F0.wireOp",EDGE,"E19")])],"isStart":false});
            var Q15;
            Q15=makeQuery(id+"F1.opExtrude","CAP_EDGE",EDGE,{"disambiguationData":[OSD([sQuery(id+"F0.wireOp",EDGE,"E19")])],"isStart":true});
            var Q16;
            Q16=makeQuery(id+"F1.opExtrude","CAP_EDGE",EDGE,{"disambiguationData":[OSD([sQuery(id+"F0.wireOp",EDGE,"E33")])],"isStart":true});
            var Q17;
            Q17=makeQuery(id+"F1.opExtrude","CAP_EDGE",EDGE,{"disambiguationData":[OSD([sQuery(id+"F0.wireOp",EDGE,"E33")])],"isStart":false});
            var Q18;
            {var subQ0=sQuery(id+"F0.wireOp",EDGE,"E9");Q18=makeQuery(id+"F1.opExtrude","CAP_EDGE",EDGE,{"disambiguationData":[OSD([subQ0]),TDD([makeQuery(id+"F0.imprint","IMPRINT",EDGE,{"disambiguationData":[TD([[makeQuery(id+"F0.imprint","INTERSECT",VERTEX,{"derivedFrom":[subQ0,sQuery(id+"F0.wireOp",EDGE,"E26")]}),1.0]])],"derivedFrom":subQ0})])],"isStart":false});}
            var Q19;
            {var subQ0=sQuery(id+"F0.wireOp",EDGE,"E9");Q19=makeQuery(id+"F1.opExtrude","CAP_EDGE",EDGE,{"disambiguationData":[OSD([subQ0]),TDD([makeQuery(id+"F0.imprint","IMPRINT",EDGE,{"disambiguationData":[TD([[makeQuery(id+"F0.imprint","INTERSECT",VERTEX,{"derivedFrom":[subQ0,sQuery(id+"F0.wireOp",EDGE,"E26")]}),1.0]])],"derivedFrom":subQ0})])],"isStart":true});}
            var Q20;
            Q20=makeQuery(id+"F1.opExtrude","CAP_EDGE",EDGE,{"disambiguationData":[OSD([sQuery(id+"F0.wireOp",EDGE,"E26")])],"isStart":false});
            var Q21;
            Q21=makeQuery(id+"F1.opExtrude","CAP_EDGE",EDGE,{"disambiguationData":[OSD([sQuery(id+"F0.wireOp",EDGE,"E26")])],"isStart":true});
            var Q22;
            Q22=makeQuery(id+"F1.opExtrude","CAP_EDGE",EDGE,{"disambiguationData":[OSD([sQuery(id+"F0.wireOp",EDGE,"E15")])],"isStart":false});
            var Q23;
            Q23=makeQuery(id+"F1.opExtrude","CAP_EDGE",EDGE,{"disambiguationData":[OSD([sQuery(id+"F0.wireOp",EDGE,"E15")])],"isStart":true});
            var Q24;
            Q24=makeQuery(id+"F1.opExtrude","CAP_EDGE",EDGE,{"disambiguationData":[OSD([sQuery(id+"F0.wireOp",EDGE,"E11.2")])],"isStart":false});
            var Q25;
            Q25=makeQuery(id+"F1.opExtrude","CAP_EDGE",EDGE,{"disambiguationData":[OSD([sQuery(id+"F0.wireOp",EDGE,"E11.2")])],"isStart":true});
            var Q26;
            Q26=makeQuery(id+"F1.opExtrude","CAP_EDGE",EDGE,{"disambiguationData":[OSD([sQuery(id+"F0.wireOp",EDGE,"E11.1")])],"isStart":true});
            var Q27;
            Q27=makeQuery(id+"F1.opExtrude","CAP_EDGE",EDGE,{"disambiguationData":[OSD([sQuery(id+"F0.wireOp",EDGE,"E11.1")])],"isStart":false});
            var Q28;
            Q28=makeQuery(id+"F1.opExtrude","CAP_EDGE",EDGE,{"disambiguationData":[OSD([sQuery(id+"F0.wireOp",EDGE,"E11.0")])],"isStart":true});
            var Q29;
            Q29=makeQuery(id+"F1.opExtrude","CAP_EDGE",EDGE,{"disambiguationData":[OSD([sQuery(id+"F0.wireOp",EDGE,"E11.0")])],"isStart":false});
            var Q30;
            Q30=makeQuery(id+"F1.opExtrude","CAP_EDGE",EDGE,{"disambiguationData":[OSD([sQuery(id+"F0.wireOp",EDGE,"E11.5")])],"isStart":false});
            var Q31;
            Q31=makeQuery(id+"F1.opExtrude","CAP_EDGE",EDGE,{"disambiguationData":[OSD([sQuery(id+"F0.wireOp",EDGE,"E11.5")])],"isStart":true});
            var Q32;
            Q32=makeQuery(id+"F1.opExtrude","CAP_EDGE",EDGE,{"disambiguationData":[OSD([sQuery(id+"F0.wireOp",EDGE,"E11.4")])],"isStart":true});
            var Q33;
            Q33=makeQuery(id+"F1.opExtrude","CAP_EDGE",EDGE,{"disambiguationData":[OSD([sQuery(id+"F0.wireOp",EDGE,"E11.4")])],"isStart":false});
            var Q34;
            Q34=makeQuery(id+"F1.opExtrude","CAP_EDGE",EDGE,{"disambiguationData":[OSD([sQuery(id+"F0.wireOp",EDGE,"E14")])],"isStart":false});
            var Q35;
            Q35=makeQuery(id+"F1.opExtrude","CAP_EDGE",EDGE,{"disambiguationData":[OSD([sQuery(id+"F0.wireOp",EDGE,"E27")])],"isStart":false});
            var Q36;
            Q36=makeQuery(id+"F1.opExtrude","CAP_EDGE",EDGE,{"disambiguationData":[OSD([sQuery(id+"F0.wireOp",EDGE,"E27")])],"isStart":true});
            var Q37;
            Q37=makeQuery(id+"F1.opExtrude","CAP_EDGE",EDGE,{"disambiguationData":[OSD([sQuery(id+"F0.wireOp",EDGE,"E14")])],"isStart":true});
            var Q38;
            {var subQ0=sQuery(id+"F0.wireOp",EDGE,"E9");Q38=makeQuery(id+"F1.opExtrude","CAP_EDGE",EDGE,{"disambiguationData":[OSD([subQ0]),TDD([makeQuery(id+"F0.imprint","IMPRINT",EDGE,{"disambiguationData":[TD([[makeQuery(id+"F0.imprint","INTERSECT",VERTEX,{"derivedFrom":[subQ0,sQuery(id+"F0.wireOp",EDGE,"E27")]}),-1.0]])],"derivedFrom":subQ0})])],"isStart":true});}
            var Q39;
            {var subQ0=sQuery(id+"F0.wireOp",EDGE,"E9");Q39=makeQuery(id+"F1.opExtrude","CAP_EDGE",EDGE,{"disambiguationData":[OSD([subQ0]),TDD([makeQuery(id+"F0.imprint","IMPRINT",EDGE,{"disambiguationData":[TD([[makeQuery(id+"F0.imprint","INTERSECT",VERTEX,{"derivedFrom":[subQ0,sQuery(id+"F0.wireOp",EDGE,"E27")]}),-1.0]])],"derivedFrom":subQ0})])],"isStart":false});}
            var Q40;
            Q40=makeQuery(id+"F1.opExtrude","CAP_EDGE",EDGE,{"disambiguationData":[OSD([sQuery(id+"F0.wireOp",EDGE,"E35")])],"isStart":false});
            var Q41;
            Q41=makeQuery(id+"F1.opExtrude","CAP_EDGE",EDGE,{"disambiguationData":[OSD([sQuery(id+"F0.wireOp",EDGE,"E35")])],"isStart":true});
            var Q42;
            Q42=makeQuery(id+"F1.opExtrude","CAP_EDGE",EDGE,{"disambiguationData":[OSD([sQuery(id+"F0.wireOp",EDGE,"E21")])],"isStart":true});
            var Q43;
            Q43=makeQuery(id+"F1.opExtrude","CAP_EDGE",EDGE,{"disambiguationData":[OSD([sQuery(id+"F0.wireOp",EDGE,"E21")])],"isStart":false});
            var Q44;
            Q44=makeQuery(id+"F1.opExtrude","CAP_EDGE",EDGE,{"disambiguationData":[OSD([sQuery(id+"F0.wireOp",EDGE,"E10.0")])],"isStart":true});
            var Q45;
            Q45=makeQuery(id+"F1.opExtrude","CAP_EDGE",EDGE,{"disambiguationData":[OSD([sQuery(id+"F0.wireOp",EDGE,"E10.0")])],"isStart":false});
            var Q46;
            Q46=makeQuery(id+"F1.opExtrude","CAP_EDGE",EDGE,{"disambiguationData":[OSD([sQuery(id+"F0.wireOp",EDGE,"E20")])],"isStart":true});
            var Q47;
            Q47=makeQuery(id+"F1.opExtrude","CAP_EDGE",EDGE,{"disambiguationData":[OSD([sQuery(id+"F0.wireOp",EDGE,"E34")])],"isStart":true});
            var Q48;
            {var subQ0=sQuery(id+"F0.wireOp",EDGE,"E9");Q48=makeQuery(id+"F1.opExtrude","CAP_EDGE",EDGE,{"disambiguationData":[OSD([subQ0]),TDD([makeQuery(id+"F0.imprint","IMPRINT",EDGE,{"disambiguationData":[TD([[makeQuery(id+"F0.imprint","INTERSECT",VERTEX,{"derivedFrom":[subQ0,sQuery(id+"F0.wireOp",EDGE,"E25")]}),1.0]])],"derivedFrom":subQ0})])],"isStart":true});}
            var Q49;
            Q49=makeQuery(id+"F1.opExtrude","CAP_EDGE",EDGE,{"disambiguationData":[OSD([sQuery(id+"F0.wireOp",EDGE,"E10.3")])],"isStart":true});
            var Q50;
            Q50=makeQuery(id+"F1.opExtrude","CAP_EDGE",EDGE,{"disambiguationData":[OSD([sQuery(id+"F0.wireOp",EDGE,"E10.4")])],"isStart":true});
            var Q51;
            Q51=makeQuery(id+"F1.opExtrude","CAP_EDGE",EDGE,{"disambiguationData":[OSD([sQuery(id+"F0.wireOp",EDGE,"E10.5")])],"isStart":true});
            var Q52;
            Q52=makeQuery(id+"F1.opExtrude","CAP_EDGE",EDGE,{"disambiguationData":[OSD([sQuery(id+"F0.wireOp",EDGE,"E20")])],"isStart":false});
            var Q53;
            Q53=makeQuery(id+"F1.opExtrude","CAP_EDGE",EDGE,{"disambiguationData":[OSD([sQuery(id+"F0.wireOp",EDGE,"E10.3")])],"isStart":false});
            var Q54;
            Q54=makeQuery(id+"F1.opExtrude","CAP_EDGE",EDGE,{"disambiguationData":[OSD([sQuery(id+"F0.wireOp",EDGE,"E10.4")])],"isStart":false});
            var Q55;
            Q55=makeQuery(id+"F1.opExtrude","CAP_EDGE",EDGE,{"disambiguationData":[OSD([sQuery(id+"F0.wireOp",EDGE,"E10.5")])],"isStart":false});
            fillet(context, id + "F4", {"entities" : qUnion([Q0, Q1, Q2, Q3, Q4, Q5, Q6, Q7, Q8, Q9, Q10, Q11, Q12, Q13, Q14, Q15, Q16, Q17, Q18, Q19, Q20, Q21, Q22, Q23, Q24, Q25, Q26, Q27, Q28, Q29, Q30, Q31, Q32, Q33, Q34, Q35, Q36, Q37, Q38, Q39, Q40, Q41, Q42, Q43, Q44, Q45, Q46, Q47, Q48, Q49, Q50, Q51, Q52, Q53, Q54, Q55]), "radius" : 2 * mm, "tangentPropagation" : true, "allowEdgeOverflow" : false});
        }
        {
            var Q0;
            Q0=makeQuery(id+"F1.opExtrude","CAP_EDGE",EDGE,{"disambiguationData":[OSD([sQuery(id+"F0.wireOp",EDGE,"E34")])],"isStart":false});
            var Q1;
            {var subQ0=sQuery(id+"F0.wireOp",EDGE,"E9");Q1=makeQuery(id+"F1.opExtrude","CAP_EDGE",EDGE,{"disambiguationData":[OSD([subQ0]),TDD([makeQuery(id+"F0.imprint","IMPRINT",EDGE,{"disambiguationData":[TD([[makeQuery(id+"F0.imprint","INTERSECT",VERTEX,{"derivedFrom":[subQ0,sQuery(id+"F0.wireOp",EDGE,"E25")]}),1.0]])],"derivedFrom":subQ0})])],"isStart":false});}
            fillet(context, id + "F5", {"entities" : qUnion([Q0, Q1]), "radius" : 2 * mm, "tangentPropagation" : true, "allowEdgeOverflow" : false});
        }
    });
